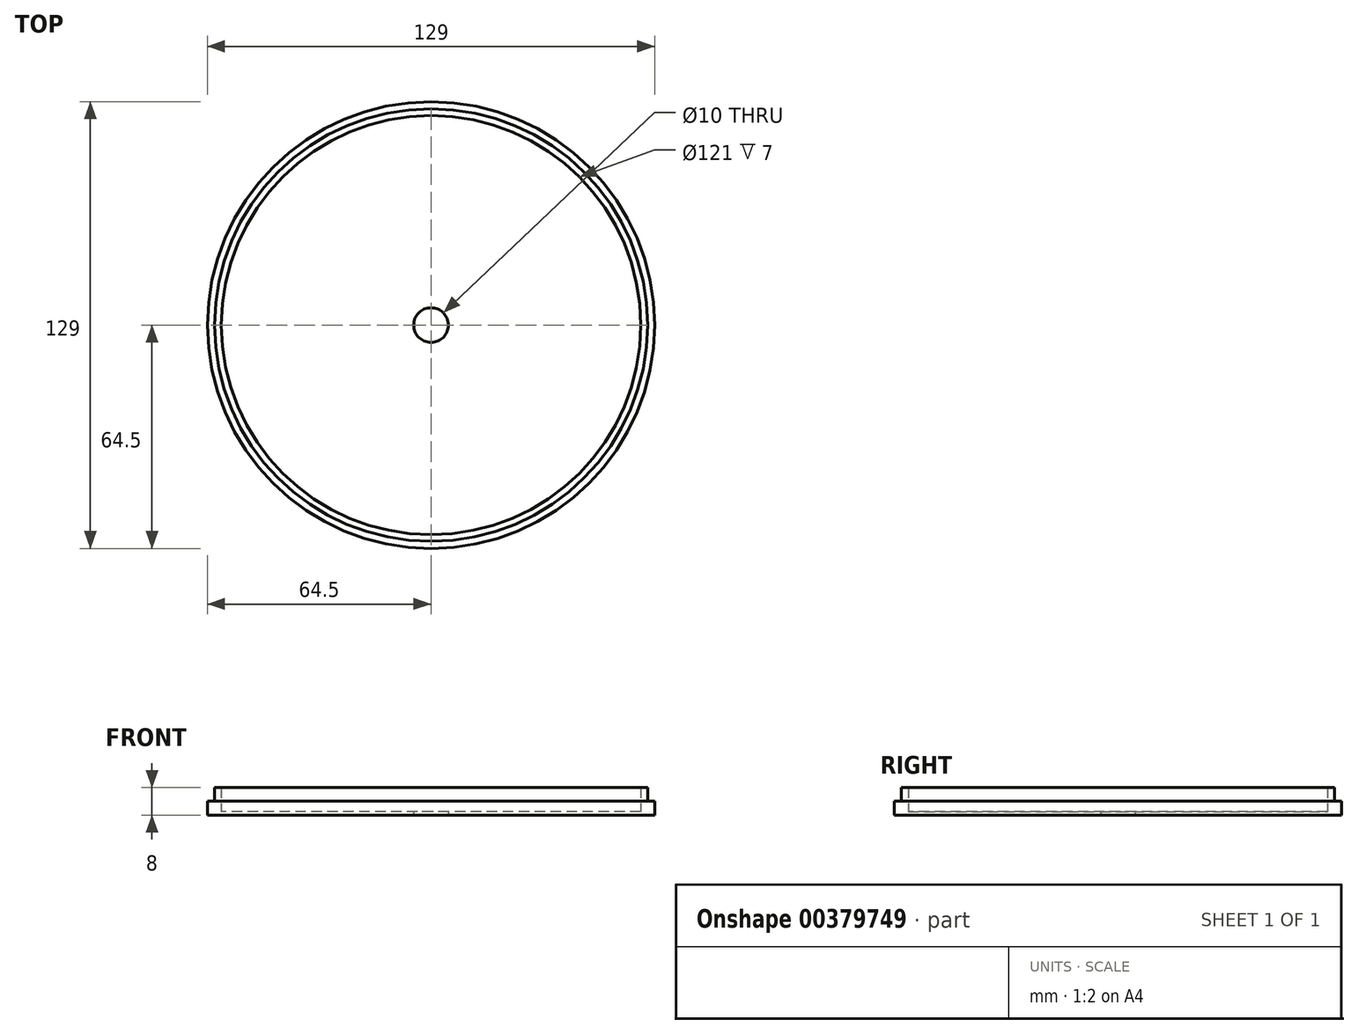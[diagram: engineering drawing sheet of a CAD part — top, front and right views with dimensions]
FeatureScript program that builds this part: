
annotation { "Feature Type Name" : "Feature", "Feature Type Description" : "" }
export const myFeature = defineFeature(function(context is Context, id is Id, definition is map)
    precondition{}
    {
        {
            var Q0;
            Q0=qCreatedBy(makeId("Top.planeOp"),FACE);
            var sketch = newSketch(context, id + "F0", { "sketchPlane" : qUnion([Q0])});
            skCircle(sketch, "E0", {"center": v(0, 0) * mm, "radius": 62.45 * mm});
            skCircle(sketch, "E1", {"center": v(0, 0) * mm, "radius": 64.5 * mm});
            skCircle(sketch, "E2", {"center": v(0, 0) * mm, "radius": 60.5 * mm});
            skCircle(sketch, "E3", {"center": v(0, 0) * mm, "radius": 5 * mm});
            skSolve(sketch);
        }
        {
            var Q0;
            Q0=makeQuery(id+"F0.imprint","IMPRINT",FACE,{"disambiguationData":[TD([[makeQuery(id+"F0.imprint","IMPRINT",EDGE,{"derivedFrom":sQuery(id+"F0.wireOp",EDGE,"E2")}),1.0]])]});
            extrude(context, id + "F1", {"entities" : qUnion([Q0]), "depth" : 1 * mm, "offsetDistance" : 25 * mm});
        }
        {
            var Q0;
            Q0=makeQuery(id+"F0.imprint","IMPRINT",FACE,{"disambiguationData":[TD([[makeQuery(id+"F0.imprint","IMPRINT",EDGE,{"derivedFrom":sQuery(id+"F0.wireOp",EDGE,"E0")}),1.0]])]});
            extrude(context, id + "F2", {"entities" : qUnion([Q0]), "operationType" : NewBodyOperationType.ADD, "depth" : 8 * mm, "offsetDistance" : 25 * mm});
        }
        {
            var Q0;
            Q0=makeQuery(id+"F0.imprint","IMPRINT",FACE,{"disambiguationData":[TD([[makeQuery(id+"F0.imprint","IMPRINT",EDGE,{"derivedFrom":sQuery(id+"F0.wireOp",EDGE,"E0")}),-1.0]])]});
            extrude(context, id + "F3", {"entities" : qUnion([Q0]), "operationType" : NewBodyOperationType.ADD, "depth" : 4 * mm, "offsetDistance" : 25 * mm});
        }
    });
